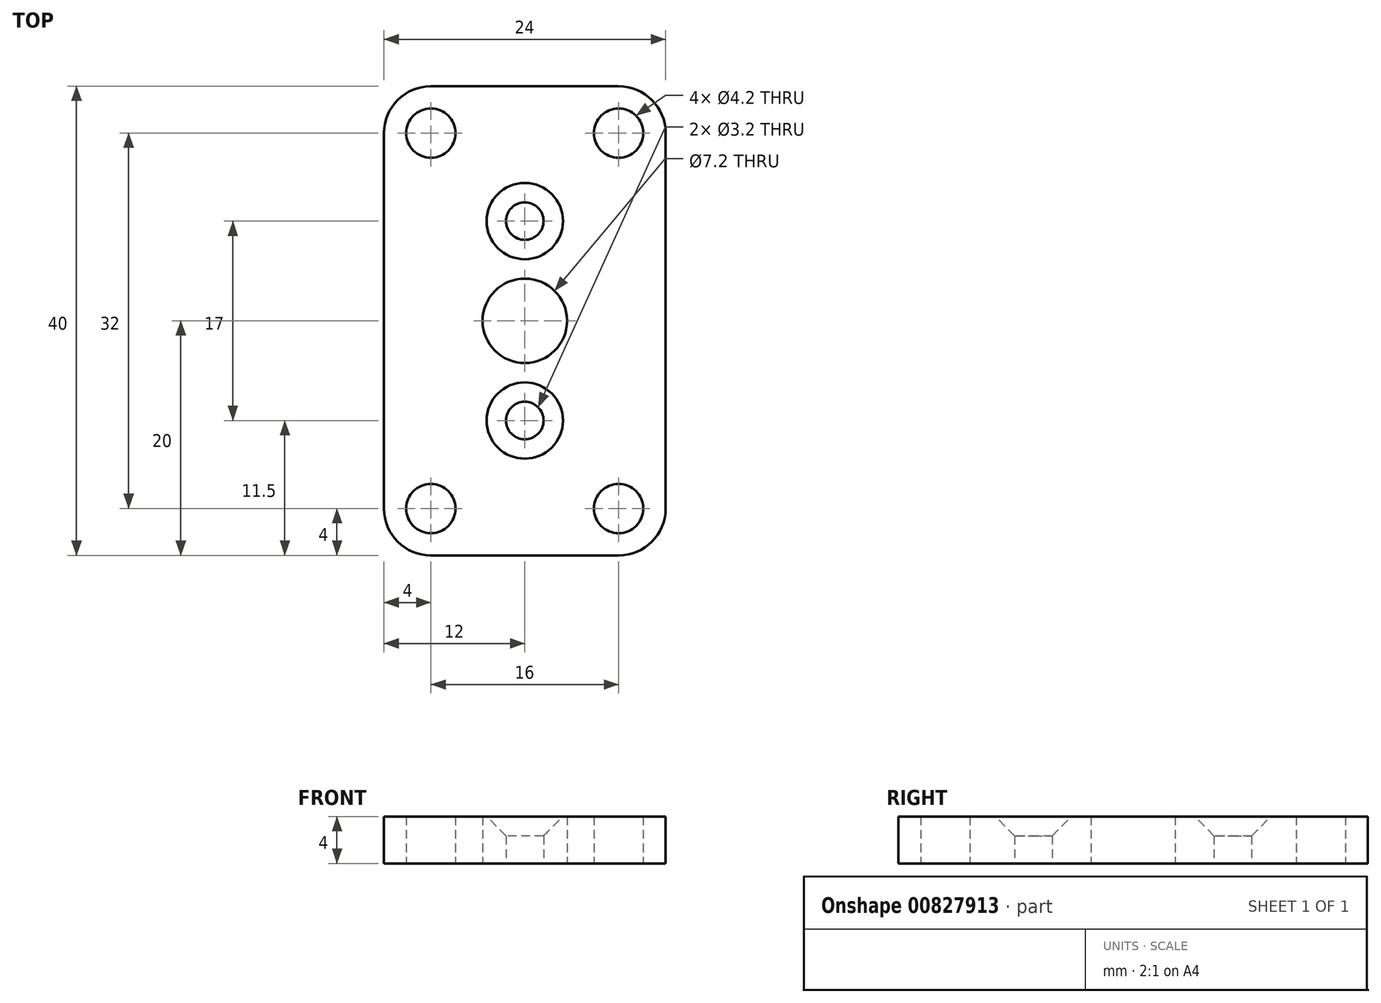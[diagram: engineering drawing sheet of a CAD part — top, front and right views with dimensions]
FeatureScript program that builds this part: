
annotation { "Feature Type Name" : "Feature", "Feature Type Description" : "" }
export const myFeature = defineFeature(function(context is Context, id is Id, definition is map)
    precondition{}
    {
        {
            var Q0;
            Q0=qCreatedBy(makeId("Top.planeOp"),FACE);
            var sketch = newSketch(context, id + "F0", { "sketchPlane" : qUnion([Q0])});
            skCircle(sketch, "E0", {"center": v(0, 0) * mm, "radius": 3.6 * mm});
            skCircle(sketch, "E1", {"center": v(0, 8.5) * mm, "radius": 1.6 * mm});
            skCircle(sketch, "E2", {"center": v(0, -8.5) * mm, "radius": 1.6 * mm});
            skLineSegment(sketch, "E3", {"start": v(0, 8.5) * mm, "end": v(0, 0) * mm, "construction": true});
            skLineSegment(sketch, "E4", {"start": v(0, 0) * mm, "end": v(0, -8.5) * mm, "construction": true});
            skLineSegment(sketch, "E5.bottom", {"start": v(-8, 16) * mm, "end": v(8, 16) * mm, "construction": true});
            skLineSegment(sketch, "E5.top", {"start": v(-8, -16) * mm, "end": v(8, -16) * mm, "construction": true});
            skLineSegment(sketch, "E5.left", {"start": v(-8, 16) * mm, "end": v(-8, -16) * mm, "construction": true});
            skLineSegment(sketch, "E5.right", {"start": v(8, 16) * mm, "end": v(8, -16) * mm, "construction": true});
            skCircle(sketch, "E6", {"center": v(8, 16) * mm, "radius": 2.1 * mm});
            skCircle(sketch, "E7", {"center": v(8, -16) * mm, "radius": 2.1 * mm});
            skCircle(sketch, "E8", {"center": v(-8, 16) * mm, "radius": 2.1 * mm});
            skCircle(sketch, "E9", {"center": v(-8, -16) * mm, "radius": 2.1 * mm});
            skLineSegment(sketch, "E10.bottom", {"start": v(8, 20) * mm, "end": v(-8, 20) * mm});
            skLineSegment(sketch, "E10.top", {"start": v(8, -20) * mm, "end": v(-8, -20) * mm});
            skLineSegment(sketch, "E10.left", {"start": v(12, 16) * mm, "end": v(12, -16) * mm});
            skLineSegment(sketch, "E10.right", {"start": v(-12, 16) * mm, "end": v(-12, -16) * mm});
            skPoint(sketch, "E11.visualSharp", {"position": v(-12, 20) * mm});
            skArc(sketch, "E11.filletArc", {"start": v(-8, 20) * mm, "mid": v(-10.83, 18.83) * mm, "end": v(-12, 16) * mm});
            skPoint(sketch, "E12.visualSharp", {"position": v(-12, -20) * mm});
            skArc(sketch, "E12.filletArc", {"start": v(-12, -16) * mm, "mid": v(-10.83, -18.83) * mm, "end": v(-8, -20) * mm});
            skPoint(sketch, "E13.visualSharp", {"position": v(12, -20) * mm});
            skArc(sketch, "E13.filletArc", {"start": v(8, -20) * mm, "mid": v(10.83, -18.83) * mm, "end": v(12, -16) * mm});
            skPoint(sketch, "E14.visualSharp", {"position": v(12, 20) * mm});
            skArc(sketch, "E14.filletArc", {"start": v(12, 16) * mm, "mid": v(10.83, 18.83) * mm, "end": v(8, 20) * mm});
            skSolve(sketch);
        }
        {
            var Q0;
            Q0=qSketchRegion(id+"F0",true);
            extrude(context, id + "F1", {"entities" : qUnion([Q0]), "depth" : 4 * mm, "offsetDistance" : 25 * mm});
        }
        {
            var Q0;
            Q0=makeQuery(id+"F1.opExtrude","CAP_EDGE",EDGE,{"disambiguationData":[OSD([sQuery(id+"F0.wireOp",EDGE,"E1")])],"isStart":false});
            var Q1;
            Q1=makeQuery(id+"F1.opExtrude","CAP_EDGE",EDGE,{"disambiguationData":[OSD([sQuery(id+"F0.wireOp",EDGE,"E2")])],"isStart":false});
            chamfer(context, id + "F2", {"entities" : qUnion([Q0, Q1]), "chamferType" : ChamferType.OFFSET_ANGLE, "width" : 1.65 * mm, "oppositeDirection" : false, "angle" : 45 * degree, "tangentPropagation" : true});
        }
    });
